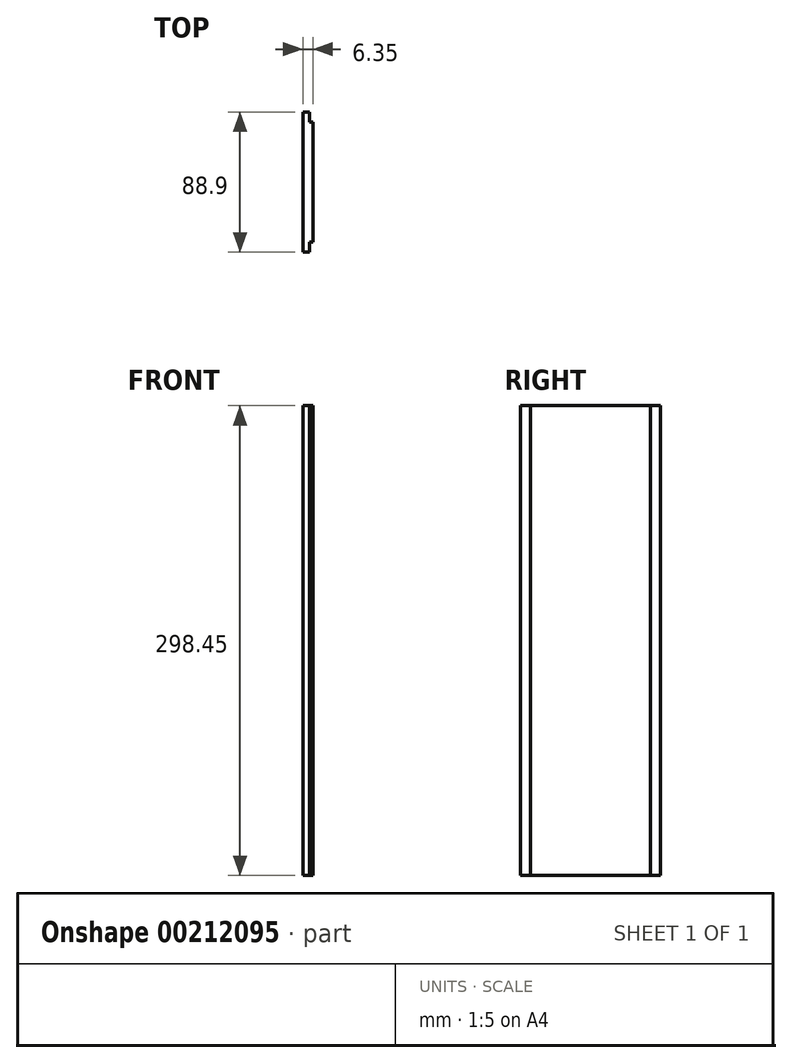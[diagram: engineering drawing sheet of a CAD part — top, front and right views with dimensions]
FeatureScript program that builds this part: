
annotation { "Feature Type Name" : "Feature", "Feature Type Description" : "" }
export const myFeature = defineFeature(function(context is Context, id is Id, definition is map)
    precondition{}
    {
        {
            var Q0;
            Q0=qCreatedBy(makeId("Right.planeOp"),FACE);
            var sketch = newSketch(context, id + "F0", { "sketchPlane" : qUnion([Q0])});
            skLineSegment(sketch, "E0.bottom", {"start": v(0, 0) * mm, "end": v(88.9, 0) * mm});
            skLineSegment(sketch, "E0.top", {"start": v(0, 298.45) * mm, "end": v(88.9, 298.45) * mm});
            skLineSegment(sketch, "E0.left", {"start": v(0, 0) * mm, "end": v(0, 298.45) * mm});
            skLineSegment(sketch, "E0.right", {"start": v(88.9, 0) * mm, "end": v(88.9, 298.45) * mm});
            skSolve(sketch);
        }
        {
            var Q0;
            Q0=qCreatedBy(makeId("Right.planeOp"),FACE);
            var sketch = newSketch(context, id + "F1", { "sketchPlane" : qUnion([Q0])});
            skLineSegment(sketch, "E1.bottom", {"start": v(6.35, 0) * mm, "end": v(82.55, 0) * mm});
            skLineSegment(sketch, "E1.top", {"start": v(6.35, 298.45) * mm, "end": v(82.55, 298.45) * mm});
            skLineSegment(sketch, "E1.left", {"start": v(6.35, 0) * mm, "end": v(6.35, 298.45) * mm});
            skLineSegment(sketch, "E1.right", {"start": v(82.55, 0) * mm, "end": v(82.55, 298.45) * mm});
            skLineSegment(sketch, "E2", {"start": v(0, 0) * mm, "end": v(6.35, 0) * mm});
            skSolve(sketch);
        }
        {
            var Q0;
            Q0 = qSketchRegion(id + "F0", true);
            extrude(context, id + "F2", {"entities" : qUnion([Q0]), "oppositeDirection" : true, "depth" : 4.23 * mm});
        }
        {
            var Q0;
            Q0 = qSketchRegion(id + "F1", true);
            extrude(context, id + "F3", {"entities" : qUnion([Q0]), "operationType" : NewBodyOperationType.ADD, "depth" : 2.12 * mm});
        }
    });
